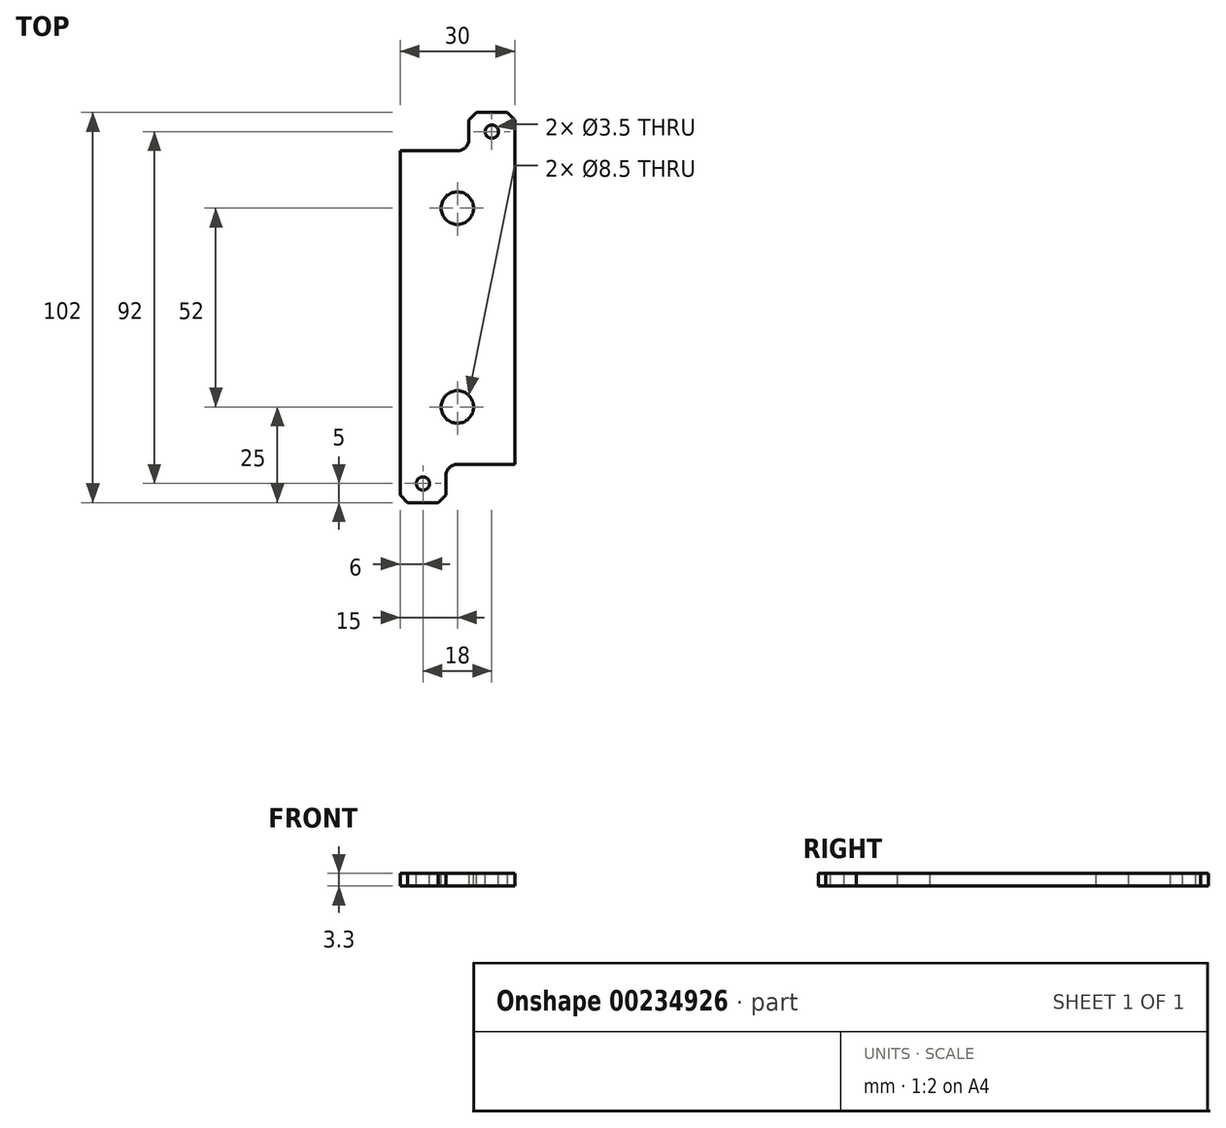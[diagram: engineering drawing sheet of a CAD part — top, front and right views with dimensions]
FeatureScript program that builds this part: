
annotation { "Feature Type Name" : "Feature", "Feature Type Description" : "" }
export const myFeature = defineFeature(function(context is Context, id is Id, definition is map)
    precondition{}
    {
        {
            var Q0;
            Q0=qCreatedBy(makeId("Top.planeOp"),FACE);
            var sketch = newSketch(context, id + "F0", { "sketchPlane" : qUnion([Q0])});
            skLineSegment(sketch, "E0.bottom", {"start": v(15, 41) * mm, "end": v(-15, 41) * mm});
            skLineSegment(sketch, "E0.top", {"start": v(15, -41) * mm, "end": v(-15, -41) * mm});
            skLineSegment(sketch, "E0.left", {"start": v(15, 41) * mm, "end": v(15, -41) * mm});
            skLineSegment(sketch, "E0.right", {"start": v(-15, 41) * mm, "end": v(-15, -41) * mm});
            skPoint(sketch, "E0.middle", {"position": v(0, 0) * mm});
            skLineSegment(sketch, "E1.bottom", {"start": v(15, 41) * mm, "end": v(3, 41) * mm});
            skLineSegment(sketch, "E1.top", {"start": v(15, 51) * mm, "end": v(3, 51) * mm});
            skLineSegment(sketch, "E1.left", {"start": v(15, 41) * mm, "end": v(15, 51) * mm});
            skLineSegment(sketch, "E1.right", {"start": v(3, 41) * mm, "end": v(3, 51) * mm});
            skLineSegment(sketch, "E2.bottom", {"start": v(-15, -41) * mm, "end": v(-3, -41) * mm});
            skLineSegment(sketch, "E2.top", {"start": v(-15, -51) * mm, "end": v(-3, -51) * mm});
            skLineSegment(sketch, "E2.left", {"start": v(-15, -41) * mm, "end": v(-15, -51) * mm});
            skLineSegment(sketch, "E2.right", {"start": v(-3, -41) * mm, "end": v(-3, -51) * mm});
            skSolve(sketch);
        }
        {
            var Q0;
            Q0=qSketchRegion(id+"F0",true);
            extrude(context, id + "F1", {"entities" : qUnion([Q0]), "depth" : 3.3 * mm});
        }
        {
            var Q0;
            Q0=makeQuery(id+"F1.opExtrude","SWEPT_EDGE",EDGE,{"disambiguationData":[OSD([sQuery(id+"F0.wireOp",EDGE,"E1.top"),sQuery(id+"F0.wireOp",EDGE,"E1.left")])]});
            var Q1;
            Q1=makeQuery(id+"F1.opExtrude","SWEPT_EDGE",EDGE,{"disambiguationData":[OSD([sQuery(id+"F0.wireOp",EDGE,"E1.top"),sQuery(id+"F0.wireOp",EDGE,"E1.right")])]});
            var Q2;
            Q2=makeQuery(id+"F1.opExtrude","SWEPT_EDGE",EDGE,{"disambiguationData":[OSD([sQuery(id+"F0.wireOp",EDGE,"E2.top"),sQuery(id+"F0.wireOp",EDGE,"E2.left")])]});
            var Q3;
            Q3=makeQuery(id+"F1.opExtrude","SWEPT_EDGE",EDGE,{"disambiguationData":[OSD([sQuery(id+"F0.wireOp",EDGE,"E2.top"),sQuery(id+"F0.wireOp",EDGE,"E2.right")])]});
            chamfer(context, id + "F2", {"entities" : qUnion([Q0, Q1, Q2, Q3]), "width" : 2 * mm, "tangentPropagation" : true});
        }
        {
            var Q0;
            Q0=makeQuery(id+"F1.opExtrude","SWEPT_EDGE",EDGE,{"disambiguationData":[OSD([sQuery(id+"F0.wireOp",EDGE,"E0.bottom"),sQuery(id+"F0.wireOp",EDGE,"E1.bottom"),sQuery(id+"F0.wireOp",EDGE,"E1.right")])]});
            fillet(context, id + "F3", {"entities" : qUnion([Q0]), "radius" : 3 * mm, "tangentPropagation" : true, "allowEdgeOverflow" : false});
        }
        {
            var Q0;
            Q0=makeQuery(id+"F1.opExtrude","SWEPT_EDGE",EDGE,{"disambiguationData":[OSD([sQuery(id+"F0.wireOp",EDGE,"E0.top"),sQuery(id+"F0.wireOp",EDGE,"E2.bottom"),sQuery(id+"F0.wireOp",EDGE,"E2.right")])]});
            fillet(context, id + "F4", {"entities" : qUnion([Q0]), "radius" : 3 * mm, "tangentPropagation" : true, "allowEdgeOverflow" : false});
        }
        {
            var Q0;
            Q0=makeQuery(id+"F1.opExtrude","CAP_FACE",FACE,{"disambiguationData":[OSD([sQuery(id+"F0.wireOp",EDGE,"E0.bottom"),sQuery(id+"F0.wireOp",EDGE,"E0.top"),sQuery(id+"F0.wireOp",EDGE,"E0.left"),sQuery(id+"F0.wireOp",EDGE,"E0.right"),sQuery(id+"F0.wireOp",EDGE,"E1.top"),sQuery(id+"F0.wireOp",EDGE,"E1.left"),sQuery(id+"F0.wireOp",EDGE,"E1.right"),sQuery(id+"F0.wireOp",EDGE,"E2.top"),sQuery(id+"F0.wireOp",EDGE,"E2.left"),sQuery(id+"F0.wireOp",EDGE,"E2.right")])],"isStart":false});
            var sketch = newSketch(context, id + "F5", { "sketchPlane" : qUnion([Q0])});
            skLineSegment(sketch, "E3", {"start": v(9, 51) * mm, "end": v(9, 41) * mm, "construction": true});
            skCircle(sketch, "E4", {"center": v(9, 46) * mm, "radius": 1.75 * mm});
            skLineSegment(sketch, "E5", {"start": v(-9, -51) * mm, "end": v(-9, -41) * mm, "construction": true});
            skCircle(sketch, "E6", {"center": v(-9, -46) * mm, "radius": 1.75 * mm});
            skSolve(sketch);
        }
        {
            var Q0;
            Q0=qSketchRegion(id+"F5",true);
            extrude(context, id + "F6", {"entities" : qUnion([Q0]), "operationType" : NewBodyOperationType.REMOVE, "oppositeDirection" : true, "depth" : 25 * mm});
        }
        {
            var Q0;
            Q0=makeQuery(id+"F1.opExtrude","CAP_FACE",FACE,{"disambiguationData":[OSD([sQuery(id+"F0.wireOp",EDGE,"E0.bottom"),sQuery(id+"F0.wireOp",EDGE,"E0.top"),sQuery(id+"F0.wireOp",EDGE,"E0.left"),sQuery(id+"F0.wireOp",EDGE,"E0.right"),sQuery(id+"F0.wireOp",EDGE,"E1.top"),sQuery(id+"F0.wireOp",EDGE,"E1.left"),sQuery(id+"F0.wireOp",EDGE,"E1.right"),sQuery(id+"F0.wireOp",EDGE,"E2.top"),sQuery(id+"F0.wireOp",EDGE,"E2.left"),sQuery(id+"F0.wireOp",EDGE,"E2.right")])],"isStart":false});
            var sketch = newSketch(context, id + "F7", { "sketchPlane" : qUnion([Q0])});
            skLineSegment(sketch, "E7", {"start": v(0, 41) * mm, "end": v(0, 0) * mm, "construction": true});
            skLineSegment(sketch, "E8", {"start": v(0, 0) * mm, "end": v(0, -41) * mm, "construction": true});
            skCircle(sketch, "E9", {"center": v(0, 26) * mm, "radius": 2.5 * mm});
            skCircle(sketch, "E10", {"center": v(0, -26) * mm, "radius": 2.5 * mm});
            skSolve(sketch);
        }
        {
            var Q0;
            Q0=qSketchRegion(id+"F7",true);
            extrude(context, id + "F8", {"entities" : qUnion([Q0]), "operationType" : NewBodyOperationType.REMOVE, "oppositeDirection" : true, "depth" : 25 * mm});
        }
        {
            var Q0;
            Q0=makeQuery(id+"F1.opExtrude","CAP_FACE",FACE,{"disambiguationData":[OSD([sQuery(id+"F0.wireOp",EDGE,"E0.bottom"),sQuery(id+"F0.wireOp",EDGE,"E0.top"),sQuery(id+"F0.wireOp",EDGE,"E0.left"),sQuery(id+"F0.wireOp",EDGE,"E0.right"),sQuery(id+"F0.wireOp",EDGE,"E1.top"),sQuery(id+"F0.wireOp",EDGE,"E1.left"),sQuery(id+"F0.wireOp",EDGE,"E1.right"),sQuery(id+"F0.wireOp",EDGE,"E2.top"),sQuery(id+"F0.wireOp",EDGE,"E2.left"),sQuery(id+"F0.wireOp",EDGE,"E2.right")])],"isStart":false});
            var sketch = newSketch(context, id + "F9", { "sketchPlane" : qUnion([Q0])});
            skCircle(sketch, "E11", {"center": v(0, 26) * mm, "radius": 4.25 * mm});
            skCircle(sketch, "E12", {"center": v(0, -26) * mm, "radius": 4.25 * mm});
            skSolve(sketch);
        }
        {
            var Q0;
            Q0 = qSketchRegion(id + "F9", true);
            extrude(context, id + "F10", {"entities" : qUnion([Q0]), "operationType" : NewBodyOperationType.REMOVE, "oppositeDirection" : true, "depth" : 25 * mm, "offsetDistance" : 25 * mm});
        }
    });
